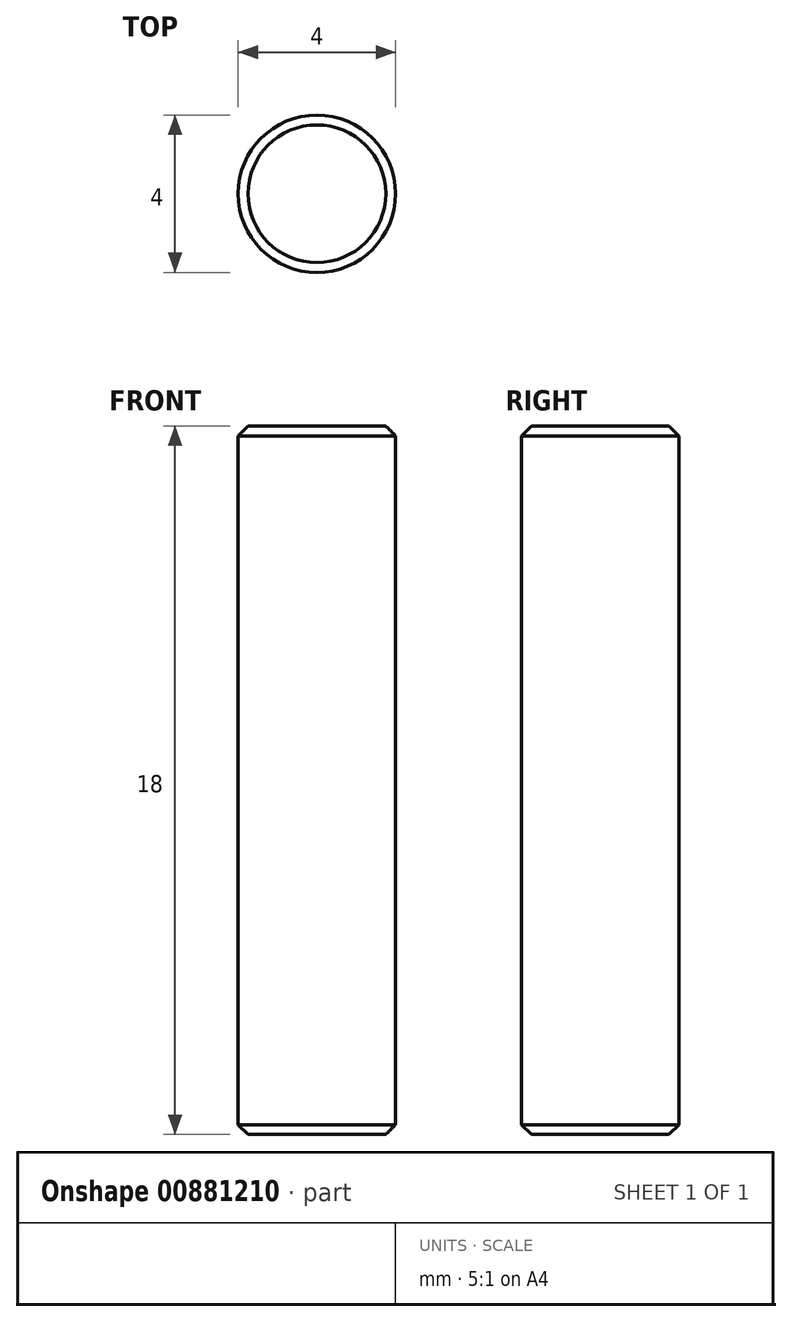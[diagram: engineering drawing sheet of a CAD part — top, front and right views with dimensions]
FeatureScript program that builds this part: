
annotation { "Feature Type Name" : "Feature", "Feature Type Description" : "" }
export const myFeature = defineFeature(function(context is Context, id is Id, definition is map)
    precondition{}
    {
        {
            var Q0;
            Q0=qCreatedBy(makeId("Top.planeOp"),FACE);
            var sketch = newSketch(context, id + "F0", { "sketchPlane" : qUnion([Q0])});
            skCircle(sketch, "E0", {"center": v(0, 0) * mm, "radius": 2 * mm});
            skSolve(sketch);
        }
        {
            var Q0;
            Q0=makeQuery(id+"F0.imprint","IMPRINT",FACE,{"disambiguationData":[TD([[makeQuery(id+"F0.imprint","IMPRINT",EDGE,{"derivedFrom":sQuery(id+"F0.wireOp",EDGE,"E0")}),1.0]])]});
            extrude(context, id + "F1", {"entities" : qUnion([Q0]), "depth" : 18 * mm, "offsetDistance" : 25 * mm});
        }
        {
            var Q0;
            Q0=makeQuery(id+"F1.opExtrude","CAP_FACE",FACE,{"disambiguationData":[OSD([sQuery(id+"F0.wireOp",EDGE,"E0")])],"isStart":false});
            var Q1;
            Q1=makeQuery(id+"F1.opExtrude","CAP_FACE",FACE,{"disambiguationData":[OSD([sQuery(id+"F0.wireOp",EDGE,"E0")])],"isStart":true});
            chamfer(context, id + "F2", {"entities" : qUnion([Q0, Q1]), "width" : 0.25 * mm, "tangentPropagation" : true});
        }
    });
